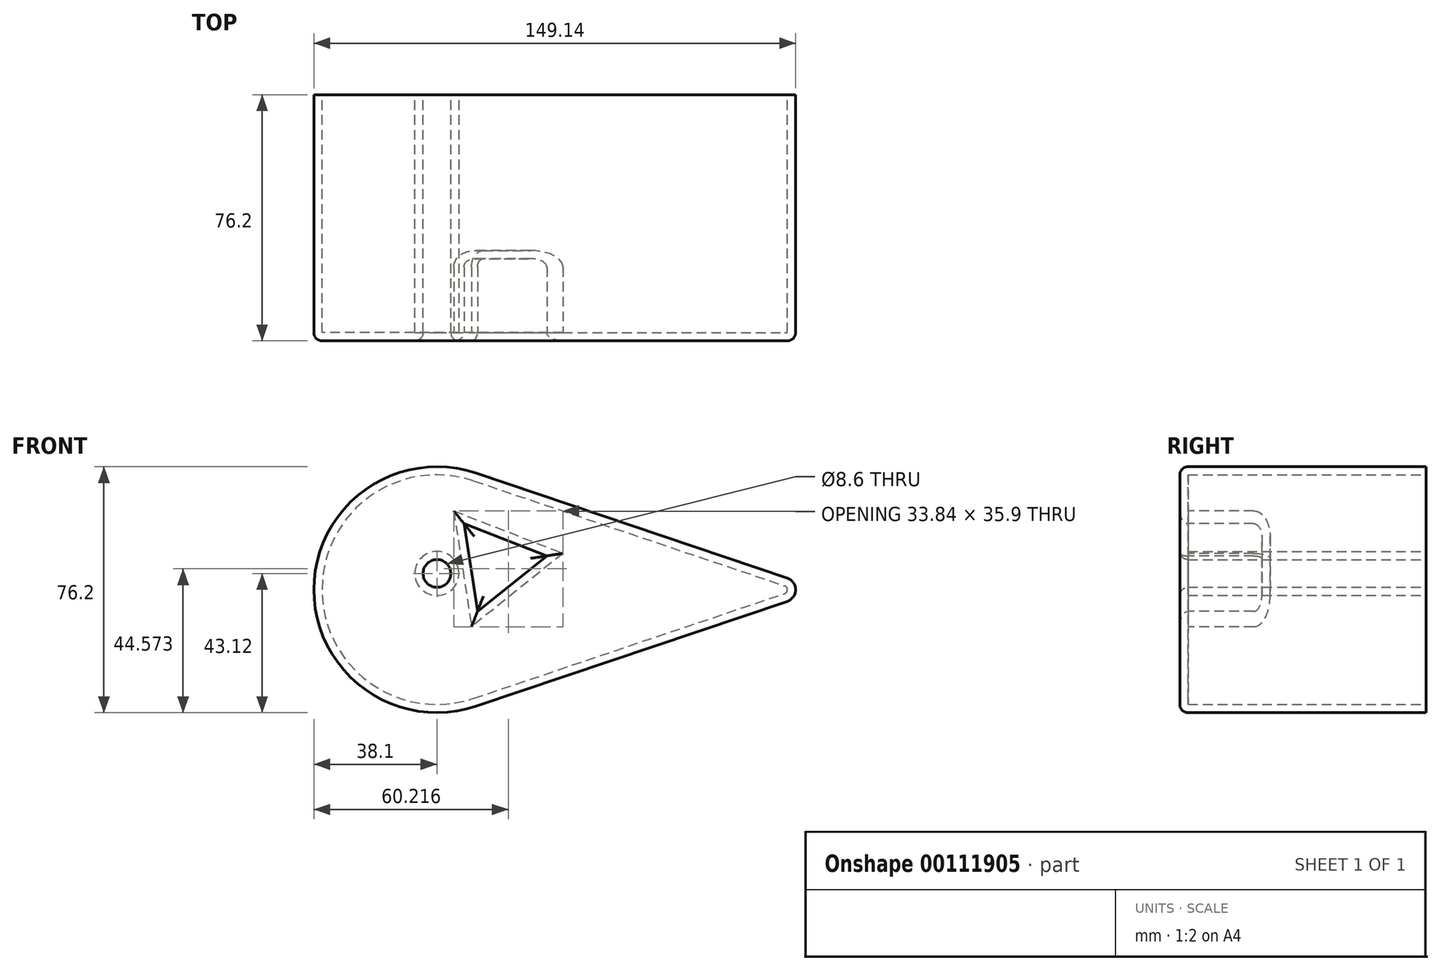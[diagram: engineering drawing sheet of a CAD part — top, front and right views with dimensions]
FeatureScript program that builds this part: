
annotation { "Feature Type Name" : "Feature", "Feature Type Description" : "" }
export const myFeature = defineFeature(function(context is Context, id is Id, definition is map)
    precondition{}
    {
        {
            var Q0;
            Q0=qCreatedBy(makeId("Front.planeOp"),FACE);
            var sketch = newSketch(context, id + "F0", { "sketchPlane" : qUnion([Q0])});
            skCircle(sketch, "E0", {"center": v(0, 0) * mm, "radius": 38.1 * mm});
            skCircle(sketch, "E1", {"center": v(0, 5.02) * mm, "radius": 4.3 * mm});
            skCircle(sketch, "E2", {"center": v(107.23, 0) * mm, "radius": 3.81 * mm});
            skLineSegment(sketch, "E3", {"start": v(12.18, 36.1) * mm, "end": v(108.45, 3.6) * mm});
            skLineSegment(sketch, "E4", {"start": v(12.18, -36.1) * mm, "end": v(108.45, -3.6) * mm});
            skLineSegment(sketch, "E5", {"start": v(-60.5, 27.87) * mm, "end": v(-60.5, 0) * mm});
            skLineSegment(sketch, "E6", {"start": v(-60.5, 0) * mm, "end": v(-39.39, 0) * mm});
            skLineSegment(sketch, "E7", {"start": v(-39.39, 17.77) * mm, "end": v(-39.39, 0) * mm});
            skLineSegment(sketch, "E8", {"start": v(-43.18, 27.87) * mm, "end": v(-39.39, 17.77) * mm});
            skSolve(sketch);
        }
        {
            var Q0;
            {var subQ0=sQuery(id+"F0.wireOp",EDGE,"E0");var subQ1=makeQuery(id+"F0.imprint","INTERSECT",VERTEX,{"derivedFrom":[subQ0,sQuery(id+"F0.wireOp",EDGE,"E3")]});Q0=makeQuery(id+"F0.imprint","IMPRINT",FACE,{"disambiguationData":[TD([[makeQuery(id+"F0.imprint","IMPRINT",EDGE,{"disambiguationData":[TD([[subQ1,-1.0]])],"derivedFrom":subQ0}),1.0]])]});}
            var Q1;
            {var subQ0=sQuery(id+"F0.wireOp",EDGE,"E2");var subQ1=makeQuery(id+"F0.imprint","INTERSECT",VERTEX,{"derivedFrom":[subQ0,sQuery(id+"F0.wireOp",EDGE,"E3")]});Q1=makeQuery(id+"F0.imprint","IMPRINT",FACE,{"disambiguationData":[TD([[makeQuery(id+"F0.imprint","IMPRINT",EDGE,{"disambiguationData":[TD([[subQ1,-1.0]])],"derivedFrom":subQ0}),1.0]])]});}
            var Q2;
            {var subQ0=sQuery(id+"F0.wireOp",EDGE,"E3");Q2=makeQuery(id+"F0.imprint","IMPRINT",FACE,{"disambiguationData":[TD([[makeQuery(id+"F0.imprint","IMPRINT",EDGE,{"derivedFrom":subQ0}),-1.0]])]});}
            extrude(context, id + "F1", {"entities" : qUnion([Q0, Q1, Q2]), "depth" : 76.2 * mm});
        }
        {
            var Q0;
            Q0=sQuery(id+"F0.wireOp",EDGE,"E1");
            extrude(context, id + "F2", {"bodyType" : ToolBodyType.SURFACE, "surfaceEntities" : qUnion([Q0]), "depth" : 25.4 * mm});
        }
        {
            var Q0;
            Q0=makeQuery(id+"F1.opExtrude","CAP_FACE",FACE,{"disambiguationData":[OSD([sQuery(id+"F0.wireOp",EDGE,"E0"),sQuery(id+"F0.wireOp",EDGE,"E1"),sQuery(id+"F0.wireOp",EDGE,"E2"),sQuery(id+"F0.wireOp",EDGE,"E3"),sQuery(id+"F0.wireOp",EDGE,"E4")])],"isStart":false});
            var sketch = newSketch(context, id + "F3", { "sketchPlane" : qUnion([Q0])});
            skCircle(sketch, "E9.cCircle", {"center": v(18.31, 8.06) * mm, "radius": 7.94 * mm, "construction": true});
            skLineSegment(sketch, "E9.0", {"start": v(8.37, 20.46) * mm, "end": v(34.02, 10.47) * mm});
            skLineSegment(sketch, "E9.1", {"start": v(34.02, 10.47) * mm, "end": v(12.55, -6.74) * mm});
            skLineSegment(sketch, "E9.2", {"start": v(12.55, -6.74) * mm, "end": v(8.37, 20.46) * mm});
            skPoint(sketch, "E9.0.midPoint", {"position": v(21.2, 15.47) * mm});
            skSolve(sketch);
        }
        {
            var Q0;
            Q0=makeQuery(id+"F3.imprint","IMPRINT",FACE,{"disambiguationData":[TD([[makeQuery(id+"F3.imprint","IMPRINT",EDGE,{"derivedFrom":sQuery(id+"F3.wireOp",EDGE,"E9.0")}),-1.0]])]});
            var Q1;
            Q1=sQuery(id+"F3.wireOp",EDGE,"E9.1");
            var Q2;
            Q2=sQuery(id+"F3.wireOp",EDGE,"E9.0");
            var Q3;
            Q3=sQuery(id+"F3.wireOp",EDGE,"E9.2");
            extrude(context, id + "F4", {"entities" : qUnion([Q0]), "operationType" : NewBodyOperationType.REMOVE, "surfaceEntities" : qUnion([Q1, Q2, Q3]), "oppositeDirection" : true, "depth" : 25.4 * mm});
        }
        {
            var Q0;
            Q0=makeQuery(id+"F1.opExtrude","CAP_FACE",FACE,{"disambiguationData":[OSD([sQuery(id+"F0.wireOp",EDGE,"E0"),sQuery(id+"F0.wireOp",EDGE,"E1"),sQuery(id+"F0.wireOp",EDGE,"E2"),sQuery(id+"F0.wireOp",EDGE,"E3"),sQuery(id+"F0.wireOp",EDGE,"E4")])],"isStart":false});
            var Q1;
            Q1=makeQuery(id+"F4.boolean.opBoolean","COPY",FACE,{"derivedFrom":makeQuery(id+"F4.opExtrude","CAP_FACE",FACE,{"disambiguationData":[OSD([sQuery(id+"F3.wireOp",EDGE,"E9.0"),sQuery(id+"F3.wireOp",EDGE,"E9.1"),sQuery(id+"F3.wireOp",EDGE,"E9.2")])],"isStart":false})});
            fillet(context, id + "F5", {"entities" : qUnion([Q0, Q1]), "radius" : 2.54 * mm, "tangentPropagation" : true, "allowEdgeOverflow" : false});
        }
        {
            var Q0;
            Q0=makeQuery(id+"F1.opExtrude","CAP_FACE",FACE,{"disambiguationData":[OSD([sQuery(id+"F0.wireOp",EDGE,"E0"),sQuery(id+"F0.wireOp",EDGE,"E1"),sQuery(id+"F0.wireOp",EDGE,"E2"),sQuery(id+"F0.wireOp",EDGE,"E3"),sQuery(id+"F0.wireOp",EDGE,"E4")])],"isStart":true});
            shell(context, id + "F6", {"entities" : qUnion([Q0]), "thickness" : 2.54 * mm});
        }
    });
